# Revit family: WSL_A3-UK-Skylight
name_source: partatom
category: Windows
revit_build: Autodesk Revit 2016 (Build: 20150220_1215(x64)
units: mm (PartAtom-declared; Revit-internal decimal feet)

## family parameters
Always vertical = No
Cut with Voids When Loaded = No
Host = Roof
Room Calculation Point = No
Shared = No

## types (2) — shared parameters
Material Flashing = Metal - Lead
Material Frame = Metal - Bronze,LightBrush
Material Glass = Glass
Material Ironmongery = Metal - Aluminium
Material Sash = Window Frame
Upstand = 25 mm  [stored 0.082021 ft]
Vert Bar Thickness = 25 mm  [stored 0.082021 ft]
Vis - Plan View = Yes

## per-type parameters (varying)
| type | Assembly Code | Height | Rough Height | Rough Width | Vis - Ironmongery | Vis - Vert Bar | Width |
| UK_Skylight 850 x 550mm | B3020110 | 850 mm  [stored 2.78871 ft] | 850 mm  [stored 2.78871 ft] | 550 mm | Yes | Yes | 550 mm |
| 660 x 1180mm |  | 1180 mm  [stored 3.87139 ft] | 1180 mm  [stored 3.87139 ft] | 660 mm | No | No | 660 mm |

note: [stored X ft] marks values corroborated as IEEE doubles in the binary element streams (Revit-internal decimal feet)

## geometry (parser evidence)
native form markers: Extrusion x1, Sweep x3
no freeform markers — native parametric forms only
